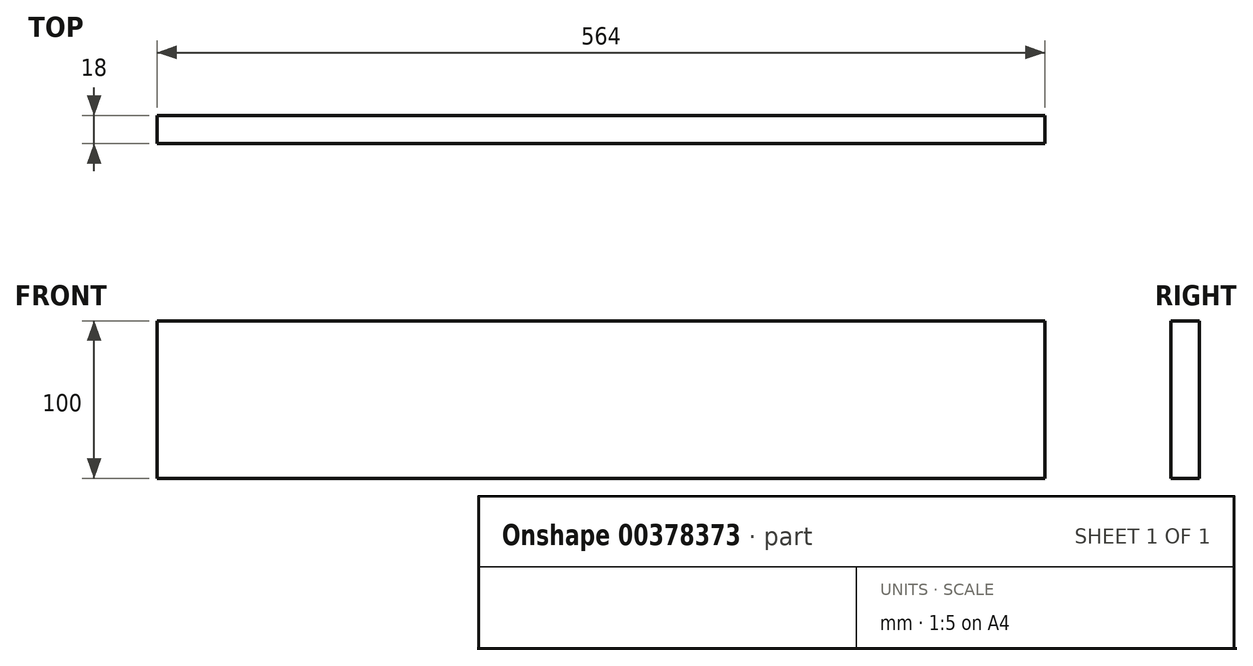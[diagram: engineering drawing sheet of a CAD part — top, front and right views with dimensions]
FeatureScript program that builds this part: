
annotation { "Feature Type Name" : "Feature", "Feature Type Description" : "" }
export const myFeature = defineFeature(function(context is Context, id is Id, definition is map)
    precondition{}
    {
        {
            var Q0;
            Q0=qCreatedBy(makeId("Right.planeOp"),FACE);
            var sketch = newSketch(context, id + "F0", { "sketchPlane" : qUnion([Q0])});
            skLineSegment(sketch, "E0.bottom", {"start": v(9, 50) * mm, "end": v(-9, 50) * mm});
            skLineSegment(sketch, "E0.top", {"start": v(9, -50) * mm, "end": v(-9, -50) * mm});
            skLineSegment(sketch, "E0.left", {"start": v(9, 50) * mm, "end": v(9, -50) * mm});
            skLineSegment(sketch, "E0.right", {"start": v(-9, 50) * mm, "end": v(-9, -50) * mm});
            skPoint(sketch, "E0.middle", {"position": v(0, 0) * mm});
            skSolve(sketch);
        }
        {
            var Q0;
            Q0=qSketchRegion(id+"F0",true);
            extrude(context, id + "F1", {"entities" : qUnion([Q0]), "depth" : 564 * mm});
        }
    });
